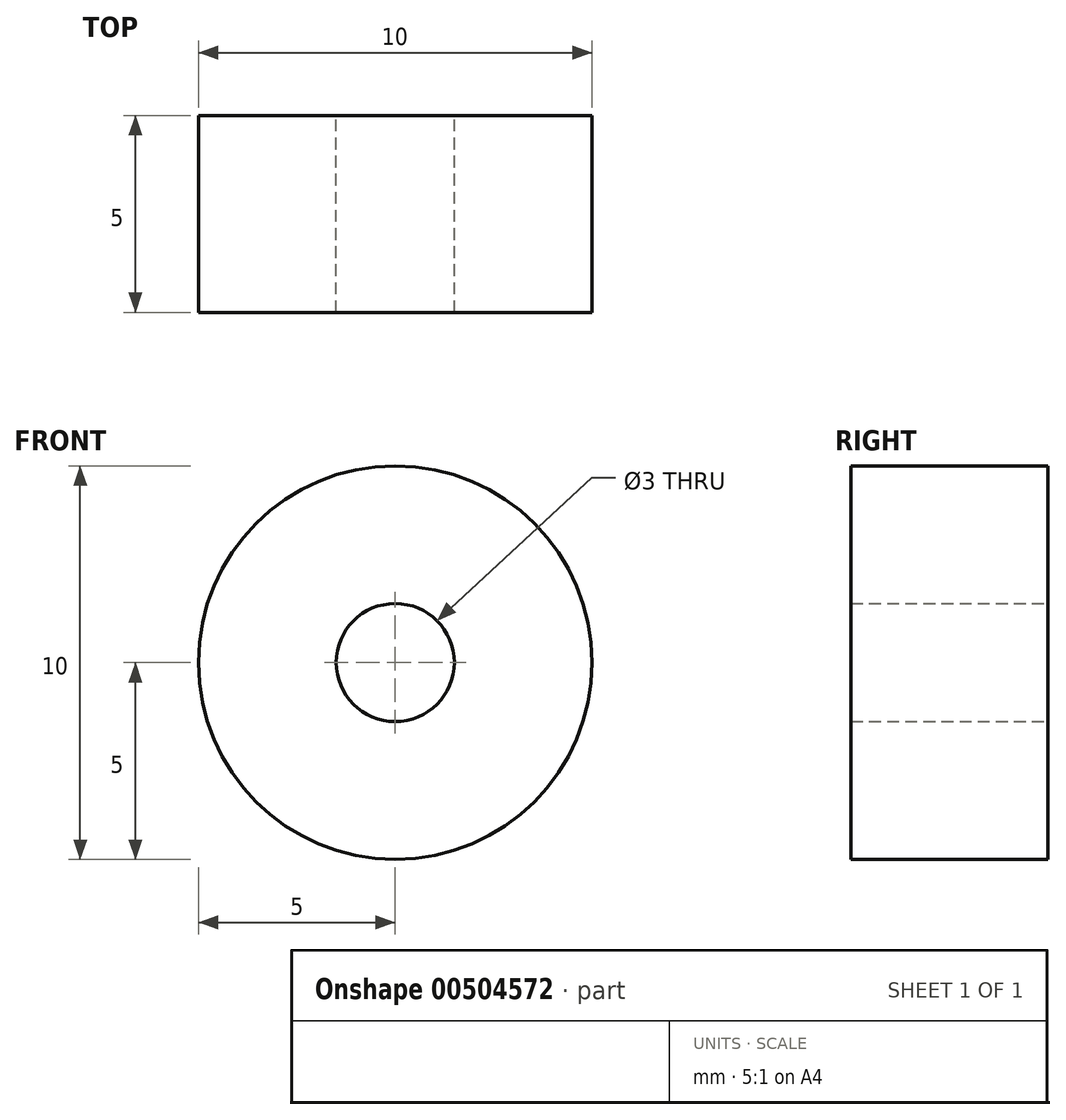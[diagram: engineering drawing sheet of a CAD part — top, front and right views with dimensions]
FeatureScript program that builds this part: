
annotation { "Feature Type Name" : "Feature", "Feature Type Description" : "" }
export const myFeature = defineFeature(function(context is Context, id is Id, definition is map)
    precondition{}
    {
        {
            var Q0;
            Q0=qCreatedBy(makeId("Front.planeOp"),FACE);
            var sketch = newSketch(context, id + "F0", { "sketchPlane" : qUnion([Q0])});
            skCircle(sketch, "E0", {"center": v(0, 0) * mm, "radius": 5 * mm});
            skCircle(sketch, "E1", {"center": v(0, 0) * mm, "radius": 1.5 * mm});
            skSolve(sketch);
        }
        {
            var Q0;
            Q0=makeQuery(id+"F0.imprint","IMPRINT",FACE,{"disambiguationData":[TD([[makeQuery(id+"F0.imprint","IMPRINT",EDGE,{"derivedFrom":sQuery(id+"F0.wireOp",EDGE,"E0")}),1.0]])]});
            extrude(context, id + "F1", {"entities" : qUnion([Q0]), "depth" : 5 * mm, "offsetDistance" : 25 * mm});
        }
    });
